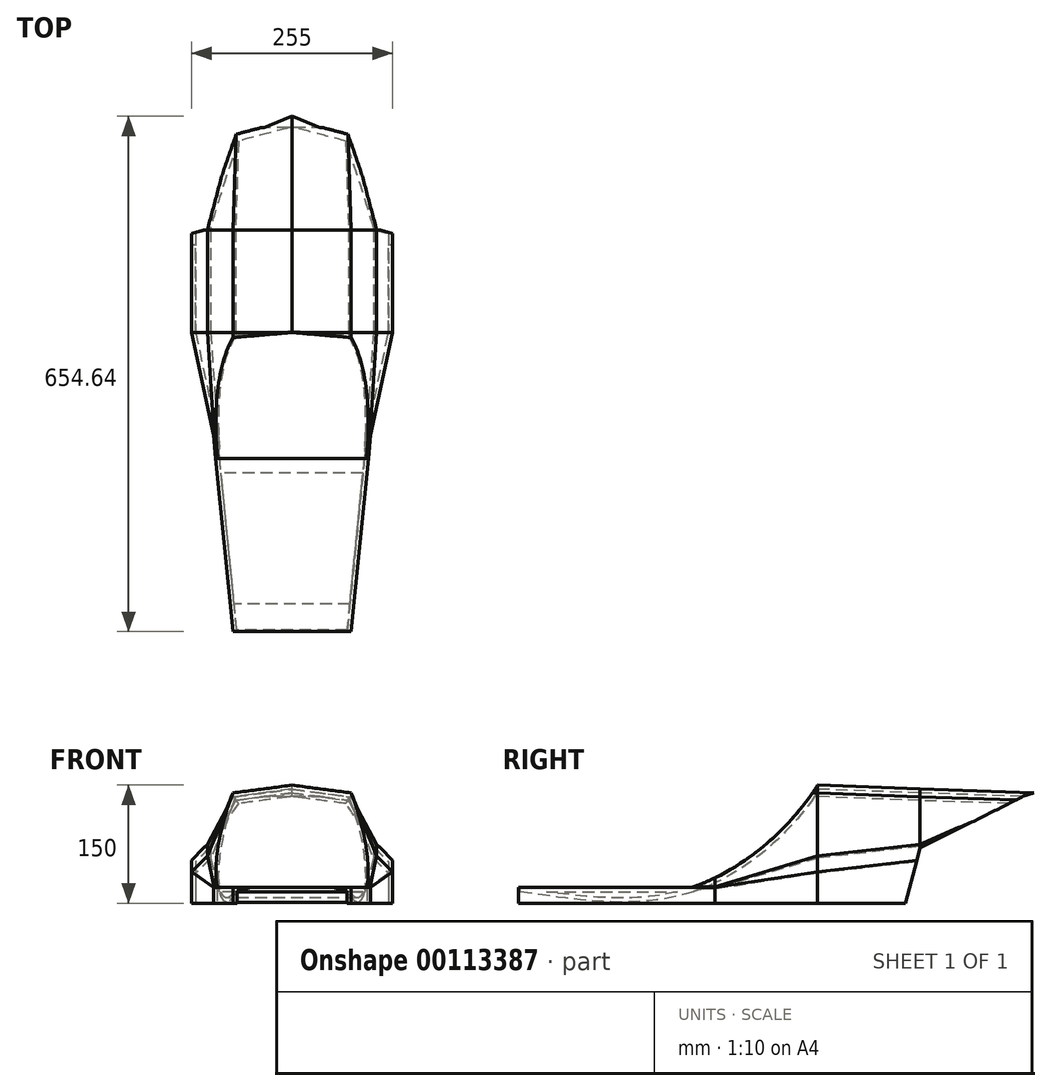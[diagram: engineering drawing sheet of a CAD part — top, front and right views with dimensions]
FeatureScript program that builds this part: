
annotation { "Feature Type Name" : "Feature", "Feature Type Description" : "" }
export const myFeature = defineFeature(function(context is Context, id is Id, definition is map)
    precondition{}
    {
        {
            var Q0;
            Q0=qCreatedBy(makeId("Front.planeOp"),FACE);
            cPlane(context, id + "F0", {"entities" : qUnion([Q0]), "cplaneType" : CPlaneType.OFFSET, "offset" : 380 * mm, "oppositeDirection" : true, "width" : 150 * mm, "height" : 150 * mm});
        }
        {
            var Q0;
            Q0=qCreatedBy(id+"F0.planeOp",FACE);
            cPlane(context, id + "F1", {"entities" : qUnion([Q0]), "cplaneType" : CPlaneType.OFFSET, "offset" : 130 * mm, "oppositeDirection" : true, "width" : 150 * mm, "height" : 150 * mm});
        }
        {
            var Q0;
            Q0=qCreatedBy(id+"F1.planeOp",FACE);
            cPlane(context, id + "F2", {"entities" : qUnion([Q0]), "cplaneType" : CPlaneType.OFFSET, "offset" : 150 * mm, "oppositeDirection" : true, "width" : 150 * mm, "height" : 150 * mm});
        }
        {
            var Q0;
            Q0=qCreatedBy(makeId("Front.planeOp"),FACE);
            cPlane(context, id + "F3", {"entities" : qUnion([Q0]), "cplaneType" : CPlaneType.OFFSET, "offset" : 250 * mm, "oppositeDirection" : true, "width" : 150 * mm, "height" : 150 * mm});
        }
        {
            var Q0;
            Q0=qCreatedBy(id+"F2.planeOp",FACE);
            var sketch = newSketch(context, id + "F4", { "sketchPlane" : qUnion([Q0])});
            skLineSegment(sketch, "E0.bottom", {"start": v(0, 0) * mm, "end": v(-127.5, 0) * mm, "construction": true});
            skLineSegment(sketch, "E0.top", {"start": v(0, 160) * mm, "end": v(-127.5, 160) * mm, "construction": true});
            skLineSegment(sketch, "E0.left", {"start": v(0, 0) * mm, "end": v(0, 160) * mm, "construction": true});
            skLineSegment(sketch, "E0.right", {"start": v(-127.5, 0) * mm, "end": v(-127.5, 160) * mm, "construction": true});
            skLineSegment(sketch, "E1.bottom", {"start": v(0, 160) * mm, "end": v(-70, 160) * mm, "construction": true});
            skLineSegment(sketch, "E1.top", {"start": v(0, 150) * mm, "end": v(-70, 150) * mm, "construction": true});
            skLineSegment(sketch, "E1.left", {"start": v(0, 160) * mm, "end": v(0, 150) * mm, "construction": true});
            skLineSegment(sketch, "E1.right", {"start": v(-70, 160) * mm, "end": v(-70, 150) * mm, "construction": true});
            skLineSegment(sketch, "E2.bottom", {"start": v(-127.5, 0) * mm, "end": v(-107.5, 0) * mm, "construction": true});
            skLineSegment(sketch, "E2.top", {"start": v(-127.5, 65) * mm, "end": v(-107.5, 65) * mm, "construction": true});
            skLineSegment(sketch, "E2.left", {"start": v(-127.5, 0) * mm, "end": v(-127.5, 65) * mm, "construction": true});
            skLineSegment(sketch, "E2.right", {"start": v(-107.5, 0) * mm, "end": v(-107.5, 65) * mm, "construction": true});
            skLineSegment(sketch, "E3.bottom", {"start": v(-107.5, 65) * mm, "end": v(-87.5, 65) * mm, "construction": true});
            skLineSegment(sketch, "E3.top", {"start": v(-107.5, 90) * mm, "end": v(-87.5, 90) * mm, "construction": true});
            skLineSegment(sketch, "E3.left", {"start": v(-107.5, 65) * mm, "end": v(-107.5, 90) * mm, "construction": true});
            skLineSegment(sketch, "E3.right", {"start": v(-87.5, 65) * mm, "end": v(-87.5, 90) * mm, "construction": true});
            skLineSegment(sketch, "E4", {"start": v(0, 160) * mm, "end": v(-70, 150) * mm});
            skLineSegment(sketch, "E5", {"start": v(-70, 150) * mm, "end": v(-107.5, 90) * mm});
            skLineSegment(sketch, "E6", {"start": v(-107.5, 90) * mm, "end": v(-127.5, 65) * mm});
            skLineSegment(sketch, "E7", {"start": v(-127.5, 65) * mm, "end": v(-127.5, 0) * mm});
            skLineSegment(sketch, "E8.MirrorCS", {"start": v(127.5, 0) * mm, "end": v(107.5, 0) * mm, "construction": true});
            skLineSegment(sketch, "E9.MirrorCS", {"start": v(127.5, 0) * mm, "end": v(127.5, 65) * mm, "construction": true});
            skLineSegment(sketch, "E10.MirrorCS", {"start": v(70, 160) * mm, "end": v(70, 150) * mm, "construction": true});
            skLineSegment(sketch, "E11.MirrorCS", {"start": v(0, 150) * mm, "end": v(70, 150) * mm, "construction": true});
            skLineSegment(sketch, "E12.MirrorCS", {"start": v(0, 160) * mm, "end": v(70, 160) * mm, "construction": true});
            skLineSegment(sketch, "E13.MirrorCS", {"start": v(127.5, 65) * mm, "end": v(107.5, 65) * mm, "construction": true});
            skLineSegment(sketch, "E14.MirrorCS", {"start": v(127.5, 0) * mm, "end": v(127.5, 160) * mm, "construction": true});
            skLineSegment(sketch, "E15.MirrorCS", {"start": v(0, 160) * mm, "end": v(127.5, 160) * mm, "construction": true});
            skLineSegment(sketch, "E16.MirrorCS", {"start": v(0, 0) * mm, "end": v(127.5, 0) * mm, "construction": true});
            skLineSegment(sketch, "E17.MirrorCS", {"start": v(87.5, 65) * mm, "end": v(87.5, 90) * mm, "construction": true});
            skLineSegment(sketch, "E18.MirrorCS", {"start": v(127.5, 65) * mm, "end": v(127.5, 0) * mm});
            skLineSegment(sketch, "E19.MirrorCS", {"start": v(107.5, 0) * mm, "end": v(107.5, 65) * mm, "construction": true});
            skLineSegment(sketch, "E20.MirrorCS", {"start": v(107.5, 65) * mm, "end": v(87.5, 65) * mm, "construction": true});
            skLineSegment(sketch, "E21.MirrorCS", {"start": v(0, 160) * mm, "end": v(70, 150) * mm});
            skLineSegment(sketch, "E22.MirrorCS", {"start": v(107.5, 65) * mm, "end": v(107.5, 90) * mm, "construction": true});
            skLineSegment(sketch, "E23.MirrorCS", {"start": v(107.5, 90) * mm, "end": v(87.5, 90) * mm, "construction": true});
            skLineSegment(sketch, "E24.MirrorCS", {"start": v(70, 150) * mm, "end": v(107.5, 90) * mm});
            skLineSegment(sketch, "E25.MirrorCS", {"start": v(107.5, 90) * mm, "end": v(127.5, 65) * mm});
            skLineSegment(sketch, "E26.0", {"start": v(122.5, 63.25) * mm, "end": v(122.5, 0) * mm});
            skLineSegment(sketch, "E26.1", {"start": v(103.41, 87.1) * mm, "end": v(122.5, 63.25) * mm});
            skLineSegment(sketch, "E26.2", {"start": v(67, 145.38) * mm, "end": v(103.41, 87.1) * mm});
            skLineSegment(sketch, "E26.3", {"start": v(0, 154.95) * mm, "end": v(67, 145.38) * mm});
            skLineSegment(sketch, "E26.4", {"start": v(-122.5, 63.25) * mm, "end": v(-122.5, 0) * mm});
            skLineSegment(sketch, "E26.5", {"start": v(-103.41, 87.1) * mm, "end": v(-122.5, 63.25) * mm});
            skLineSegment(sketch, "E26.6", {"start": v(-67, 145.38) * mm, "end": v(-103.41, 87.1) * mm});
            skLineSegment(sketch, "E26.7", {"start": v(0, 154.95) * mm, "end": v(-67, 145.38) * mm});
            skLineSegment(sketch, "E27", {"start": v(127.5, 0) * mm, "end": v(122.5, 0) * mm});
            skLineSegment(sketch, "E28", {"start": v(-122.5, 0) * mm, "end": v(-127.5, 0) * mm});
            skSolve(sketch);
        }
        {
            var Q0;
            Q0=qCreatedBy(id+"F1.planeOp",FACE);
            var sketch = newSketch(context, id + "F5", { "sketchPlane" : qUnion([Q0])});
            skLineSegment(sketch, "E29.bottom", {"start": v(0, 0) * mm, "end": v(-127.5, 0) * mm, "construction": true});
            skLineSegment(sketch, "E29.top", {"start": v(0, 165) * mm, "end": v(-127.5, 165) * mm, "construction": true});
            skLineSegment(sketch, "E29.left", {"start": v(0, 0) * mm, "end": v(0, 165) * mm, "construction": true});
            skLineSegment(sketch, "E29.right", {"start": v(-127.5, 0) * mm, "end": v(-127.5, 165) * mm, "construction": true});
            skLineSegment(sketch, "E30.bottom", {"start": v(0, 165) * mm, "end": v(-75, 165) * mm, "construction": true});
            skLineSegment(sketch, "E30.top", {"start": v(0, 155) * mm, "end": v(-75, 155) * mm, "construction": true});
            skLineSegment(sketch, "E30.left", {"start": v(0, 165) * mm, "end": v(0, 155) * mm, "construction": true});
            skLineSegment(sketch, "E30.right", {"start": v(-75, 165) * mm, "end": v(-75, 155) * mm, "construction": true});
            skLineSegment(sketch, "E31.bottom", {"start": v(-127.5, 0) * mm, "end": v(-107.5, 0) * mm, "construction": true});
            skLineSegment(sketch, "E31.top", {"start": v(-127.5, 75) * mm, "end": v(-107.5, 75) * mm, "construction": true});
            skLineSegment(sketch, "E31.left", {"start": v(-127.5, 0) * mm, "end": v(-127.5, 75) * mm, "construction": true});
            skLineSegment(sketch, "E31.right", {"start": v(-107.5, 0) * mm, "end": v(-107.5, 75) * mm, "construction": true});
            skLineSegment(sketch, "E32.bottom", {"start": v(-107.5, 75) * mm, "end": v(-87.5, 75) * mm, "construction": true});
            skLineSegment(sketch, "E32.top", {"start": v(-107.5, 95) * mm, "end": v(-87.5, 95) * mm, "construction": true});
            skLineSegment(sketch, "E32.left", {"start": v(-107.5, 75) * mm, "end": v(-107.5, 95) * mm, "construction": true});
            skLineSegment(sketch, "E32.right", {"start": v(-87.5, 75) * mm, "end": v(-87.5, 95) * mm, "construction": true});
            skLineSegment(sketch, "E33", {"start": v(0, 165) * mm, "end": v(-75, 155) * mm});
            skLineSegment(sketch, "E34", {"start": v(-75, 155) * mm, "end": v(-107.5, 95) * mm});
            skLineSegment(sketch, "E35", {"start": v(-107.5, 95) * mm, "end": v(-127.5, 75) * mm});
            skLineSegment(sketch, "E36", {"start": v(-127.5, 75) * mm, "end": v(-127.5, 0) * mm});
            skLineSegment(sketch, "E37.MirrorCS", {"start": v(127.5, 0) * mm, "end": v(107.5, 0) * mm, "construction": true});
            skLineSegment(sketch, "E38.MirrorCS", {"start": v(127.5, 0) * mm, "end": v(127.5, 75) * mm, "construction": true});
            skLineSegment(sketch, "E39.MirrorCS", {"start": v(75, 165) * mm, "end": v(75, 155) * mm, "construction": true});
            skLineSegment(sketch, "E40.MirrorCS", {"start": v(0, 155) * mm, "end": v(75, 155) * mm, "construction": true});
            skLineSegment(sketch, "E41.MirrorCS", {"start": v(0, 165) * mm, "end": v(75, 165) * mm, "construction": true});
            skLineSegment(sketch, "E42.MirrorCS", {"start": v(127.5, 75) * mm, "end": v(107.5, 75) * mm, "construction": true});
            skLineSegment(sketch, "E43.MirrorCS", {"start": v(127.5, 0) * mm, "end": v(127.5, 165) * mm, "construction": true});
            skLineSegment(sketch, "E44.MirrorCS", {"start": v(0, 165) * mm, "end": v(127.5, 165) * mm, "construction": true});
            skLineSegment(sketch, "E45.MirrorCS", {"start": v(0, 0) * mm, "end": v(127.5, 0) * mm, "construction": true});
            skLineSegment(sketch, "E46.MirrorCS", {"start": v(87.5, 75) * mm, "end": v(87.5, 95) * mm, "construction": true});
            skLineSegment(sketch, "E47.MirrorCS", {"start": v(127.5, 75) * mm, "end": v(127.5, 0) * mm});
            skLineSegment(sketch, "E48.MirrorCS", {"start": v(107.5, 0) * mm, "end": v(107.5, 75) * mm, "construction": true});
            skLineSegment(sketch, "E49.MirrorCS", {"start": v(107.5, 75) * mm, "end": v(87.5, 75) * mm, "construction": true});
            skLineSegment(sketch, "E50.MirrorCS", {"start": v(0, 165) * mm, "end": v(75, 155) * mm});
            skLineSegment(sketch, "E51.MirrorCS", {"start": v(107.5, 75) * mm, "end": v(107.5, 95) * mm, "construction": true});
            skLineSegment(sketch, "E52.MirrorCS", {"start": v(107.5, 95) * mm, "end": v(87.5, 95) * mm, "construction": true});
            skLineSegment(sketch, "E53.MirrorCS", {"start": v(75, 155) * mm, "end": v(107.5, 95) * mm});
            skLineSegment(sketch, "E54.MirrorCS", {"start": v(107.5, 95) * mm, "end": v(127.5, 75) * mm});
            skLineSegment(sketch, "E55.0", {"start": v(122.5, 72.93) * mm, "end": v(122.5, 0) * mm});
            skLineSegment(sketch, "E55.1", {"start": v(103.45, 91.98) * mm, "end": v(122.5, 72.93) * mm});
            skLineSegment(sketch, "E55.2", {"start": v(71.82, 150.38) * mm, "end": v(103.45, 91.98) * mm});
            skLineSegment(sketch, "E55.3", {"start": v(0, 159.96) * mm, "end": v(71.82, 150.38) * mm});
            skLineSegment(sketch, "E55.4", {"start": v(-122.5, 72.93) * mm, "end": v(-122.5, 0) * mm});
            skLineSegment(sketch, "E55.5", {"start": v(-103.45, 91.98) * mm, "end": v(-122.5, 72.93) * mm});
            skLineSegment(sketch, "E55.6", {"start": v(-71.82, 150.38) * mm, "end": v(-103.45, 91.98) * mm});
            skLineSegment(sketch, "E55.7", {"start": v(0, 159.96) * mm, "end": v(-71.82, 150.38) * mm});
            skLineSegment(sketch, "E56", {"start": v(127.5, 0) * mm, "end": v(122.5, 0) * mm});
            skLineSegment(sketch, "E57", {"start": v(-122.5, 0) * mm, "end": v(-127.5, 0) * mm});
            skSolve(sketch);
        }
        {
            var Q0;
            Q0=qCreatedBy(id+"F0.planeOp",FACE);
            var sketch = newSketch(context, id + "F6", { "sketchPlane" : qUnion([Q0])});
            skLineSegment(sketch, "E58.bottom", {"start": v(0, 0) * mm, "end": v(-127.5, 0) * mm, "construction": true});
            skLineSegment(sketch, "E58.top", {"start": v(0, 170) * mm, "end": v(-127.5, 170) * mm, "construction": true});
            skLineSegment(sketch, "E58.left", {"start": v(0, 0) * mm, "end": v(0, 170) * mm, "construction": true});
            skLineSegment(sketch, "E58.right", {"start": v(-127.5, 0) * mm, "end": v(-127.5, 170) * mm, "construction": true});
            skLineSegment(sketch, "E59.bottom", {"start": v(0, 170) * mm, "end": v(-75, 170) * mm, "construction": true});
            skLineSegment(sketch, "E59.top", {"start": v(0, 160) * mm, "end": v(-75, 160) * mm, "construction": true});
            skLineSegment(sketch, "E59.left", {"start": v(0, 170) * mm, "end": v(0, 160) * mm, "construction": true});
            skLineSegment(sketch, "E59.right", {"start": v(-75, 170) * mm, "end": v(-75, 160) * mm, "construction": true});
            skLineSegment(sketch, "E60.bottom", {"start": v(-127.5, 0) * mm, "end": v(-107.5, 0) * mm, "construction": true});
            skLineSegment(sketch, "E60.top", {"start": v(-127.5, 60) * mm, "end": v(-107.5, 60) * mm, "construction": true});
            skLineSegment(sketch, "E60.left", {"start": v(-127.5, 0) * mm, "end": v(-127.5, 60) * mm, "construction": true});
            skLineSegment(sketch, "E60.right", {"start": v(-107.5, 0) * mm, "end": v(-107.5, 60) * mm, "construction": true});
            skLineSegment(sketch, "E61.bottom", {"start": v(-107.5, 60) * mm, "end": v(-87.5, 60) * mm, "construction": true});
            skLineSegment(sketch, "E61.top", {"start": v(-107.5, 80) * mm, "end": v(-87.5, 80) * mm, "construction": true});
            skLineSegment(sketch, "E61.left", {"start": v(-107.5, 60) * mm, "end": v(-107.5, 80) * mm, "construction": true});
            skLineSegment(sketch, "E61.right", {"start": v(-87.5, 60) * mm, "end": v(-87.5, 80) * mm, "construction": true});
            skLineSegment(sketch, "E62", {"start": v(0, 170) * mm, "end": v(-75, 160) * mm});
            skLineSegment(sketch, "E63", {"start": v(-75, 160) * mm, "end": v(-107.5, 80) * mm});
            skLineSegment(sketch, "E64", {"start": v(-107.5, 80) * mm, "end": v(-127.5, 60) * mm});
            skLineSegment(sketch, "E65", {"start": v(-127.5, 60) * mm, "end": v(-127.5, 0) * mm});
            skLineSegment(sketch, "E66.MirrorCS", {"start": v(127.5, 0) * mm, "end": v(107.5, 0) * mm, "construction": true});
            skLineSegment(sketch, "E67.MirrorCS", {"start": v(127.5, 0) * mm, "end": v(127.5, 60) * mm, "construction": true});
            skLineSegment(sketch, "E68.MirrorCS", {"start": v(75, 170) * mm, "end": v(75, 160) * mm, "construction": true});
            skLineSegment(sketch, "E69.MirrorCS", {"start": v(0, 160) * mm, "end": v(75, 160) * mm, "construction": true});
            skLineSegment(sketch, "E70.MirrorCS", {"start": v(0, 170) * mm, "end": v(75, 170) * mm, "construction": true});
            skLineSegment(sketch, "E71.MirrorCS", {"start": v(127.5, 60) * mm, "end": v(107.5, 60) * mm, "construction": true});
            skLineSegment(sketch, "E72.MirrorCS", {"start": v(127.5, 0) * mm, "end": v(127.5, 170) * mm, "construction": true});
            skLineSegment(sketch, "E73.MirrorCS", {"start": v(0, 170) * mm, "end": v(127.5, 170) * mm, "construction": true});
            skLineSegment(sketch, "E74.MirrorCS", {"start": v(0, 0) * mm, "end": v(127.5, 0) * mm, "construction": true});
            skLineSegment(sketch, "E75.MirrorCS", {"start": v(87.5, 60) * mm, "end": v(87.5, 80) * mm, "construction": true});
            skLineSegment(sketch, "E76.MirrorCS", {"start": v(127.5, 60) * mm, "end": v(127.5, 0) * mm});
            skLineSegment(sketch, "E77.MirrorCS", {"start": v(107.5, 0) * mm, "end": v(107.5, 60) * mm, "construction": true});
            skLineSegment(sketch, "E78.MirrorCS", {"start": v(107.5, 60) * mm, "end": v(87.5, 60) * mm, "construction": true});
            skLineSegment(sketch, "E79.MirrorCS", {"start": v(0, 170) * mm, "end": v(75, 160) * mm});
            skLineSegment(sketch, "E80.MirrorCS", {"start": v(107.5, 60) * mm, "end": v(107.5, 80) * mm, "construction": true});
            skLineSegment(sketch, "E81.MirrorCS", {"start": v(107.5, 80) * mm, "end": v(87.5, 80) * mm, "construction": true});
            skLineSegment(sketch, "E82.MirrorCS", {"start": v(75, 160) * mm, "end": v(107.5, 80) * mm});
            skLineSegment(sketch, "E83.MirrorCS", {"start": v(107.5, 80) * mm, "end": v(127.5, 60) * mm});
            skLineSegment(sketch, "E84.0", {"start": v(122.5, 57.93) * mm, "end": v(122.5, 0) * mm});
            skLineSegment(sketch, "E84.1", {"start": v(103.25, 77.18) * mm, "end": v(122.5, 57.93) * mm});
            skLineSegment(sketch, "E84.2", {"start": v(71.46, 155.43) * mm, "end": v(103.25, 77.18) * mm});
            skLineSegment(sketch, "E84.3", {"start": v(0, 164.96) * mm, "end": v(71.46, 155.43) * mm});
            skLineSegment(sketch, "E84.4", {"start": v(-122.5, 57.93) * mm, "end": v(-122.5, 0) * mm});
            skLineSegment(sketch, "E84.5", {"start": v(-103.25, 77.18) * mm, "end": v(-122.5, 57.93) * mm});
            skLineSegment(sketch, "E84.6", {"start": v(-71.46, 155.43) * mm, "end": v(-103.25, 77.18) * mm});
            skLineSegment(sketch, "E84.7", {"start": v(0, 164.96) * mm, "end": v(-71.46, 155.43) * mm});
            skLineSegment(sketch, "E85", {"start": v(127.5, 0) * mm, "end": v(122.5, 0) * mm});
            skLineSegment(sketch, "E86", {"start": v(-122.5, 0) * mm, "end": v(-127.5, 0) * mm});
            skSolve(sketch);
        }
        {
            var Q0;
            Q0=qCreatedBy(id+"F3.planeOp",FACE);
            var sketch = newSketch(context, id + "F7", { "sketchPlane" : qUnion([Q0])});
            skLineSegment(sketch, "E87.bottom", {"start": v(0, 0) * mm, "end": v(-100, 0) * mm, "construction": true});
            skLineSegment(sketch, "E87.top", {"start": v(0, 170) * mm, "end": v(-100, 170) * mm, "construction": true});
            skLineSegment(sketch, "E87.left", {"start": v(0, 0) * mm, "end": v(0, 170) * mm, "construction": true});
            skLineSegment(sketch, "E87.right", {"start": v(-100, 0) * mm, "end": v(-100, 170) * mm, "construction": true});
            skLineSegment(sketch, "E88.bottom", {"start": v(0, 170) * mm, "end": v(-75, 170) * mm, "construction": true});
            skLineSegment(sketch, "E88.top", {"start": v(0, 160) * mm, "end": v(-75, 160) * mm, "construction": true});
            skLineSegment(sketch, "E88.left", {"start": v(0, 170) * mm, "end": v(0, 160) * mm, "construction": true});
            skLineSegment(sketch, "E88.right", {"start": v(-75, 170) * mm, "end": v(-75, 160) * mm, "construction": true});
            skLineSegment(sketch, "E89.bottom", {"start": v(-100, 0) * mm, "end": v(-99, 0) * mm, "construction": true});
            skLineSegment(sketch, "E89.top", {"start": v(-100, 40) * mm, "end": v(-99, 40) * mm, "construction": true});
            skLineSegment(sketch, "E89.left", {"start": v(-100, 0) * mm, "end": v(-100, 40) * mm, "construction": true});
            skLineSegment(sketch, "E89.right", {"start": v(-99, 0) * mm, "end": v(-99, 40) * mm, "construction": true});
            skLineSegment(sketch, "E90.bottom", {"start": v(-99, 40) * mm, "end": v(-79, 40) * mm, "construction": true});
            skLineSegment(sketch, "E90.top", {"start": v(-99, 41) * mm, "end": v(-79, 41) * mm, "construction": true});
            skLineSegment(sketch, "E90.left", {"start": v(-99, 40) * mm, "end": v(-99, 41) * mm, "construction": true});
            skLineSegment(sketch, "E90.right", {"start": v(-79, 40) * mm, "end": v(-79, 41) * mm, "construction": true});
            skLineSegment(sketch, "E91", {"start": v(0, 170) * mm, "end": v(-75, 160) * mm});
            skLineSegment(sketch, "E92", {"start": v(-75, 160) * mm, "end": v(-99, 41) * mm});
            skLineSegment(sketch, "E93", {"start": v(-99, 41) * mm, "end": v(-100, 40) * mm});
            skLineSegment(sketch, "E94", {"start": v(-100, 40) * mm, "end": v(-100, 0) * mm});
            skLineSegment(sketch, "E95.MirrorCS", {"start": v(100, 0) * mm, "end": v(99, 0) * mm, "construction": true});
            skLineSegment(sketch, "E96.MirrorCS", {"start": v(100, 0) * mm, "end": v(100, 40) * mm, "construction": true});
            skLineSegment(sketch, "E97.MirrorCS", {"start": v(75, 170) * mm, "end": v(75, 160) * mm, "construction": true});
            skLineSegment(sketch, "E98.MirrorCS", {"start": v(0, 160) * mm, "end": v(75, 160) * mm, "construction": true});
            skLineSegment(sketch, "E99.MirrorCS", {"start": v(0, 170) * mm, "end": v(75, 170) * mm, "construction": true});
            skLineSegment(sketch, "E100.MirrorCS", {"start": v(100, 40) * mm, "end": v(99, 40) * mm, "construction": true});
            skLineSegment(sketch, "E101.MirrorCS", {"start": v(100, 0) * mm, "end": v(100, 170) * mm, "construction": true});
            skLineSegment(sketch, "E102.MirrorCS", {"start": v(0, 170) * mm, "end": v(100, 170) * mm, "construction": true});
            skLineSegment(sketch, "E103.MirrorCS", {"start": v(0, 0) * mm, "end": v(100, 0) * mm, "construction": true});
            skLineSegment(sketch, "E104.MirrorCS", {"start": v(79, 40) * mm, "end": v(79, 41) * mm, "construction": true});
            skLineSegment(sketch, "E105.MirrorCS", {"start": v(100, 40) * mm, "end": v(100, 0) * mm});
            skLineSegment(sketch, "E106.MirrorCS", {"start": v(99, 0) * mm, "end": v(99, 40) * mm, "construction": true});
            skLineSegment(sketch, "E107.MirrorCS", {"start": v(99, 40) * mm, "end": v(79, 40) * mm, "construction": true});
            skLineSegment(sketch, "E108.MirrorCS", {"start": v(0, 170) * mm, "end": v(75, 160) * mm});
            skLineSegment(sketch, "E109.MirrorCS", {"start": v(99, 40) * mm, "end": v(99, 41) * mm, "construction": true});
            skLineSegment(sketch, "E110.MirrorCS", {"start": v(99, 41) * mm, "end": v(79, 41) * mm, "construction": true});
            skLineSegment(sketch, "E111.MirrorCS", {"start": v(75, 160) * mm, "end": v(99, 41) * mm});
            skLineSegment(sketch, "E112.MirrorCS", {"start": v(99, 41) * mm, "end": v(100, 40) * mm});
            skLineSegment(sketch, "E113.0", {"start": v(95, 37.93) * mm, "end": v(95, 0) * mm});
            skLineSegment(sketch, "E113.1", {"start": v(94.4, 38.53) * mm, "end": v(95, 37.93) * mm});
            skLineSegment(sketch, "E113.2", {"start": v(70.8, 155.52) * mm, "end": v(94.4, 38.53) * mm});
            skLineSegment(sketch, "E113.3", {"start": v(0, 164.96) * mm, "end": v(70.8, 155.52) * mm});
            skLineSegment(sketch, "E113.4", {"start": v(-95, 37.93) * mm, "end": v(-95, 0) * mm});
            skLineSegment(sketch, "E113.5", {"start": v(-94.4, 38.53) * mm, "end": v(-95, 37.93) * mm});
            skLineSegment(sketch, "E113.6", {"start": v(-70.8, 155.52) * mm, "end": v(-94.4, 38.53) * mm});
            skLineSegment(sketch, "E113.7", {"start": v(0, 164.96) * mm, "end": v(-70.8, 155.52) * mm});
            skLineSegment(sketch, "E114", {"start": v(100, 0) * mm, "end": v(95, 0) * mm});
            skLineSegment(sketch, "E115", {"start": v(-95, 0) * mm, "end": v(-100, 0) * mm});
            skSolve(sketch);
        }
        {
            var Q0;
            Q0=qCreatedBy(makeId("Front.planeOp"),FACE);
            var sketch = newSketch(context, id + "F8", { "sketchPlane" : qUnion([Q0])});
            skLineSegment(sketch, "E116.bottom", {"start": v(0, 0) * mm, "end": v(-75, 0) * mm, "construction": true});
            skLineSegment(sketch, "E116.top", {"start": v(0, 170) * mm, "end": v(-75, 170) * mm, "construction": true});
            skLineSegment(sketch, "E116.left", {"start": v(0, 0) * mm, "end": v(0, 170) * mm, "construction": true});
            skLineSegment(sketch, "E116.right", {"start": v(-75, 0) * mm, "end": v(-75, 170) * mm, "construction": true});
            skLineSegment(sketch, "E117.bottom", {"start": v(0, 170) * mm, "end": v(-30, 170) * mm, "construction": true});
            skLineSegment(sketch, "E117.top", {"start": v(0, 160) * mm, "end": v(-30, 160) * mm, "construction": true});
            skLineSegment(sketch, "E117.left", {"start": v(0, 170) * mm, "end": v(0, 160) * mm, "construction": true});
            skLineSegment(sketch, "E117.right", {"start": v(-30, 170) * mm, "end": v(-30, 160) * mm, "construction": true});
            skLineSegment(sketch, "E118.bottom", {"start": v(-75, 0) * mm, "end": v(-60, 0) * mm, "construction": true});
            skLineSegment(sketch, "E118.top", {"start": v(-75, 40) * mm, "end": v(-60, 40) * mm, "construction": true});
            skLineSegment(sketch, "E118.left", {"start": v(-75, 0) * mm, "end": v(-75, 40) * mm, "construction": true});
            skLineSegment(sketch, "E118.right", {"start": v(-60, 0) * mm, "end": v(-60, 40) * mm, "construction": true});
            skLineSegment(sketch, "E119.bottom", {"start": v(-60, 40) * mm, "end": v(-40, 40) * mm, "construction": true});
            skLineSegment(sketch, "E119.top", {"start": v(-60, 42) * mm, "end": v(-40, 42) * mm, "construction": true});
            skLineSegment(sketch, "E119.left", {"start": v(-60, 40) * mm, "end": v(-60, 42) * mm, "construction": true});
            skLineSegment(sketch, "E119.right", {"start": v(-40, 40) * mm, "end": v(-40, 42) * mm, "construction": true});
            skLineSegment(sketch, "E120", {"start": v(0, 170) * mm, "end": v(-30, 160) * mm});
            skLineSegment(sketch, "E121", {"start": v(-30, 160) * mm, "end": v(-60, 42) * mm});
            skLineSegment(sketch, "E122", {"start": v(-60, 42) * mm, "end": v(-75, 40) * mm});
            skLineSegment(sketch, "E123", {"start": v(-75, 40) * mm, "end": v(-75, 0) * mm});
            skLineSegment(sketch, "E124.MirrorCS", {"start": v(75, 0) * mm, "end": v(60, 0) * mm, "construction": true});
            skLineSegment(sketch, "E125.MirrorCS", {"start": v(75, 0) * mm, "end": v(75, 40) * mm, "construction": true});
            skLineSegment(sketch, "E126.MirrorCS", {"start": v(30, 170) * mm, "end": v(30, 160) * mm, "construction": true});
            skLineSegment(sketch, "E127.MirrorCS", {"start": v(0, 160) * mm, "end": v(30, 160) * mm, "construction": true});
            skLineSegment(sketch, "E128.MirrorCS", {"start": v(0, 170) * mm, "end": v(30, 170) * mm, "construction": true});
            skLineSegment(sketch, "E129.MirrorCS", {"start": v(75, 40) * mm, "end": v(60, 40) * mm, "construction": true});
            skLineSegment(sketch, "E130.MirrorCS", {"start": v(75, 0) * mm, "end": v(75, 170) * mm, "construction": true});
            skLineSegment(sketch, "E131.MirrorCS", {"start": v(0, 170) * mm, "end": v(75, 170) * mm, "construction": true});
            skLineSegment(sketch, "E132.MirrorCS", {"start": v(0, 0) * mm, "end": v(75, 0) * mm, "construction": true});
            skLineSegment(sketch, "E133.MirrorCS", {"start": v(40, 40) * mm, "end": v(40, 42) * mm, "construction": true});
            skLineSegment(sketch, "E134.MirrorCS", {"start": v(75, 40) * mm, "end": v(75, 0) * mm});
            skLineSegment(sketch, "E135.MirrorCS", {"start": v(60, 0) * mm, "end": v(60, 40) * mm, "construction": true});
            skLineSegment(sketch, "E136.MirrorCS", {"start": v(60, 40) * mm, "end": v(40, 40) * mm, "construction": true});
            skLineSegment(sketch, "E137.MirrorCS", {"start": v(0, 170) * mm, "end": v(30, 160) * mm});
            skLineSegment(sketch, "E138.MirrorCS", {"start": v(60, 40) * mm, "end": v(60, 42) * mm, "construction": true});
            skLineSegment(sketch, "E139.MirrorCS", {"start": v(60, 42) * mm, "end": v(40, 42) * mm, "construction": true});
            skLineSegment(sketch, "E140.MirrorCS", {"start": v(30, 160) * mm, "end": v(60, 42) * mm});
            skLineSegment(sketch, "E141.MirrorCS", {"start": v(60, 42) * mm, "end": v(75, 40) * mm});
            skLineSegment(sketch, "E142.0", {"start": v(70, 35.62) * mm, "end": v(70, 0) * mm});
            skLineSegment(sketch, "E142.1", {"start": v(55.99, 37.5) * mm, "end": v(70, 35.62) * mm});
            skLineSegment(sketch, "E142.2", {"start": v(25.83, 156.12) * mm, "end": v(55.99, 37.5) * mm});
            skLineSegment(sketch, "E142.3", {"start": v(0, 164.73) * mm, "end": v(25.83, 156.12) * mm});
            skLineSegment(sketch, "E142.4", {"start": v(-70, 35.62) * mm, "end": v(-70, 0) * mm});
            skLineSegment(sketch, "E142.5", {"start": v(-55.99, 37.5) * mm, "end": v(-70, 35.62) * mm});
            skLineSegment(sketch, "E142.6", {"start": v(-25.83, 156.12) * mm, "end": v(-55.99, 37.5) * mm});
            skLineSegment(sketch, "E142.7", {"start": v(0, 164.73) * mm, "end": v(-25.83, 156.12) * mm});
            skLineSegment(sketch, "E143", {"start": v(75, 0) * mm, "end": v(70, 0) * mm});
            skLineSegment(sketch, "E144", {"start": v(-70, 0) * mm, "end": v(-75, 0) * mm});
            skSolve(sketch);
        }
        {
            var Q0;
            Q0=qCreatedBy(makeId("Right.planeOp"),FACE);
            var sketch = newSketch(context, id + "F9", { "sketchPlane" : qUnion([Q0])});
            skLineSegment(sketch, "E145", {"start": v(0, 0) * mm, "end": v(380, 0) * mm, "construction": true});
            skLineSegment(sketch, "E146", {"start": v(380, 0) * mm, "end": v(380, 170) * mm, "construction": true});
            skLineSegment(sketch, "E147", {"start": v(0, 0) * mm, "end": v(0, 40) * mm, "construction": true});
            skLineSegment(sketch, "E148", {"start": v(0, 40) * mm, "end": v(220, 40) * mm});
            skFitSpline(sketch, "E149", {"points": [v(380, 170) * mm, v(220, 40) * mm, v(0, 40) * mm], "startDerivative": vector(-215.96, -343.22) * mm, "endDerivative": vector(-478.3, 74.11) * mm});
            skLineSegment(sketch, "E150", {"start": v(380, 170) * mm, "end": v(380, 230.78) * mm});
            skLineSegment(sketch, "E151", {"start": v(380, 230.78) * mm, "end": v(7.34, 230.78) * mm});
            skLineSegment(sketch, "E152", {"start": v(7.34, 230.78) * mm, "end": v(-5.55, 185.11) * mm});
            skLineSegment(sketch, "E153", {"start": v(-5.55, 185.11) * mm, "end": v(0, 40) * mm});
            skSolve(sketch);
        }
        {
            var Q0;
            Q0=qCreatedBy(makeId("Right.planeOp"),FACE);
            var sketch = newSketch(context, id + "F10", { "sketchPlane" : qUnion([Q0])});
            skLineSegment(sketch, "E154", {"start": v(0, 0) * mm, "end": v(600, 0) * mm, "construction": true});
            skLineSegment(sketch, "E155", {"start": v(600, 0) * mm, "end": v(600, 40) * mm});
            skLineSegment(sketch, "E156", {"start": v(600, 40) * mm, "end": v(600, 65) * mm, "construction": true});
            skLineSegment(sketch, "E157", {"start": v(600, 65) * mm, "end": v(625, 65) * mm, "construction": true});
            skLineSegment(sketch, "E158", {"start": v(600, 40) * mm, "end": v(625, 65) * mm});
            skLineSegment(sketch, "E159", {"start": v(625, 65) * mm, "end": v(880.62, 212.2) * mm});
            skLineSegment(sketch, "E160", {"start": v(880.62, 212.2) * mm, "end": v(932.67, 242.1) * mm});
            skLineSegment(sketch, "E161", {"start": v(932.67, 242.1) * mm, "end": v(866.28, 117.59) * mm});
            skLineSegment(sketch, "E162", {"start": v(866.28, 117.59) * mm, "end": v(834.8, 61.75) * mm});
            skLineSegment(sketch, "E163", {"start": v(600, 0) * mm, "end": v(790, 0) * mm});
            skLineSegment(sketch, "E164", {"start": v(790, 0) * mm, "end": v(790, 65) * mm, "construction": true});
            skLineSegment(sketch, "E165", {"start": v(834.8, 61.75) * mm, "end": v(790, 0) * mm});
            skSolve(sketch);
        }
        {
            var Q0;
            Q0=qCreatedBy(makeId("Right.planeOp"),FACE);
            var sketch = newSketch(context, id + "F11", { "sketchPlane" : qUnion([Q0])});
            skLineSegment(sketch, "E166", {"start": v(0, 0) * mm, "end": v(380, 0) * mm, "construction": true});
            skLineSegment(sketch, "E167", {"start": v(380, 0) * mm, "end": v(380, 170) * mm, "construction": true});
            skLineSegment(sketch, "E168", {"start": v(0, 0) * mm, "end": v(0, 40) * mm, "construction": true});
            skLineSegment(sketch, "E169", {"start": v(0, 40) * mm, "end": v(220, 40) * mm});
            skFitSpline(sketch, "E170", {"points": [v(380, 170) * mm, v(220, 40) * mm, v(0, 40) * mm], "startDerivative": vector(-215.96, -343.22) * mm, "endDerivative": vector(-478.3, 74.11) * mm});
            skLineSegment(sketch, "E171", {"start": v(2.2, -5.3) * mm, "end": v(382.2, -5.3) * mm, "construction": true});
            skLineSegment(sketch, "E172", {"start": v(382.2, -5.3) * mm, "end": v(382.2, 164.7) * mm, "construction": true});
            skLineSegment(sketch, "E173", {"start": v(2.2, -5.3) * mm, "end": v(2.2, 34.7) * mm, "construction": true});
            skLineSegment(sketch, "E174", {"start": v(2.2, 34.7) * mm, "end": v(222.2, 34.7) * mm});
            skFitSpline(sketch, "E175", {"points": [v(382.2, 164.7) * mm, v(222.2, 34.7) * mm, v(2.2, 34.7) * mm], "startDerivative": vector(-215.96, -343.22) * mm, "endDerivative": vector(-478.3, 74.11) * mm});
            skLineSegment(sketch, "E176", {"start": v(2.2, 34.7) * mm, "end": v(0, 40) * mm});
            skLineSegment(sketch, "E177", {"start": v(382.2, 164.7) * mm, "end": v(380, 170) * mm});
            skSolve(sketch);
        }
        {
            var Q0;
            Q0=qSketchRegion(id+"F5",true);
            var Q1;
            Q1=qSketchRegion(id+"F6",true);
            loft(context, id + "F12", {"sheetProfilesArray" : [{ "sheetProfileEntities" : qUnion([Q0]) }, { "sheetProfileEntities" : qUnion([Q1]) }]});
        }
        {
            var Q0;
            Q0=qCreatedBy(makeId("Top.planeOp"),FACE);
            var sketch = newSketch(context, id + "F13", { "sketchPlane" : qUnion([Q0])});
            skLineSegment(sketch, "E178", {"start": v(0, 0) * mm, "end": v(0, 660) * mm, "construction": true});
            skLineSegment(sketch, "E179", {"start": v(0, 660) * mm, "end": v(-38, 660) * mm, "construction": true});
            skLineSegment(sketch, "E180", {"start": v(0, 640) * mm, "end": v(-71, 640) * mm, "construction": true});
            skLineSegment(sketch, "E181", {"start": v(-38, 660) * mm, "end": v(-71, 640) * mm});
            skLineSegment(sketch, "E182", {"start": v(-71, 640) * mm, "end": v(-71, 610) * mm, "construction": true});
            skLineSegment(sketch, "E183", {"start": v(-71, 610) * mm, "end": v(-81, 610) * mm, "construction": true});
            skLineSegment(sketch, "E184", {"start": v(-71, 640) * mm, "end": v(-81, 610) * mm});
            skLineSegment(sketch, "E185", {"start": v(-81, 610) * mm, "end": v(-81, 605) * mm, "construction": true});
            skLineSegment(sketch, "E186", {"start": v(0, 510) * mm, "end": v(-107.58, 510) * mm, "construction": true});
            skLineSegment(sketch, "E187", {"start": v(-81, 610) * mm, "end": v(-107.58, 510) * mm});
            skLineSegment(sketch, "E188", {"start": v(-107.58, 510) * mm, "end": v(-166.67, 510) * mm});
            skLineSegment(sketch, "E189", {"start": v(-166.67, 510) * mm, "end": v(-157.39, 706.64) * mm});
            skLineSegment(sketch, "E190", {"start": v(-157.39, 706.64) * mm, "end": v(-38, 660) * mm});
            skLineSegment(sketch, "E191.MirrorCS", {"start": v(81, 610) * mm, "end": v(81, 610) * mm});
            skLineSegment(sketch, "E192.MirrorCS", {"start": v(81, 610) * mm, "end": v(81, 605) * mm, "construction": true});
            skLineSegment(sketch, "E193.MirrorCS", {"start": v(81, 605) * mm, "end": v(81, 610) * mm, "construction": true});
            skLineSegment(sketch, "E194.MirrorCS", {"start": v(71, 610) * mm, "end": v(81, 610) * mm, "construction": true});
            skLineSegment(sketch, "E195.MirrorCS", {"start": v(71, 640) * mm, "end": v(71, 610) * mm, "construction": true});
            skLineSegment(sketch, "E196.MirrorCS", {"start": v(0, 660) * mm, "end": v(38, 660) * mm, "construction": true});
            skLineSegment(sketch, "E197.MirrorCS", {"start": v(71, 640) * mm, "end": v(81, 610) * mm});
            skLineSegment(sketch, "E198.MirrorCS", {"start": v(166.67, 510) * mm, "end": v(157.39, 706.64) * mm});
            skLineSegment(sketch, "E199.MirrorCS", {"start": v(0, 640) * mm, "end": v(71, 640) * mm, "construction": true});
            skLineSegment(sketch, "E200.MirrorCS", {"start": v(0, 510) * mm, "end": v(107.58, 510) * mm, "construction": true});
            skLineSegment(sketch, "E201.MirrorCS", {"start": v(38, 660) * mm, "end": v(71, 640) * mm});
            skLineSegment(sketch, "E202.MirrorCS", {"start": v(81, 610) * mm, "end": v(107.58, 510) * mm});
            skLineSegment(sketch, "E203.MirrorCS", {"start": v(157.39, 706.64) * mm, "end": v(38, 660) * mm});
            skLineSegment(sketch, "E204.MirrorCS", {"start": v(107.58, 510) * mm, "end": v(166.67, 510) * mm});
            skSolve(sketch);
        }
        {
            var Q0;
            Q0=qCreatedBy(makeId("Right.planeOp"),FACE);
            var sketch = newSketch(context, id + "F14", { "sketchPlane" : qUnion([Q0])});
            skLineSegment(sketch, "E205", {"start": v(0, 0) * mm, "end": v(0, 20) * mm});
            skLineSegment(sketch, "E206", {"start": v(0, 20) * mm, "end": v(550.35, 20) * mm});
            skLineSegment(sketch, "E207", {"start": v(550.35, 20) * mm, "end": v(550.35, 0) * mm});
            skLineSegment(sketch, "E208", {"start": v(550.35, 0) * mm, "end": v(0, 0) * mm});
            skSolve(sketch);
        }
        {
            var Q0;
            Q0=makeQuery(id+"F9.imprint","IMPRINT",FACE,{"disambiguationData":[TD([[makeQuery(id+"F9.imprint","IMPRINT",EDGE,{"derivedFrom":sQuery(id+"F9.wireOp",EDGE,"E148")}),1.0]])]});
            extrude(context, id + "F15", {"entities" : qUnion([Q0]), "operationType" : NewBodyOperationType.REMOVE, "oppositeDirection" : true, "depth" : 200 * mm, "hasSecondDirection" : true, "secondDirectionOppositeDirection" : false, "secondDirectionDepth" : 200 * mm});
        }
        {
            var Q1;
            Q1 = qSketchRegion(id + "F4", true);
            var Q2;
            Q2 = qSketchRegion(id + "F5", true);
            loft(context, id + "F16", {"operationType" : NewBodyOperationType.ADD, "sheetProfilesArray" : [{ "sheetProfileEntities" : qUnion([Q1]) }, { "sheetProfileEntities" : qUnion([Q2]) }]});
        }
        {
            var Q0;
            Q0 = qSketchRegion(id + "F13", true);
            extrude(context, id + "F17", {"entities" : qUnion([Q0]), "operationType" : NewBodyOperationType.REMOVE, "depth" : 200 * mm});
        }
        {
            var Q0;
            Q0=qCreatedBy(makeId("Right.planeOp"),FACE);
            var sketch = newSketch(context, id + "F18", { "sketchPlane" : qUnion([Q0])});
            skLineSegment(sketch, "E209", {"start": v(0, 0) * mm, "end": v(510, 0) * mm, "construction": true});
            skLineSegment(sketch, "E210", {"start": v(510, 0) * mm, "end": v(510, 90) * mm, "construction": true});
            skLineSegment(sketch, "E211", {"start": v(510, 0) * mm, "end": v(640, 0) * mm});
            skLineSegment(sketch, "E212", {"start": v(640, 0) * mm, "end": v(640, 155) * mm, "construction": true});
            skLineSegment(sketch, "E213", {"start": v(510, 90) * mm, "end": v(640, 155) * mm});
            skLineSegment(sketch, "E214", {"start": v(640, 0) * mm, "end": v(640.2, 0) * mm});
            skLineSegment(sketch, "E215", {"start": v(640.2, 0) * mm, "end": v(640.2, 155.65) * mm, "construction": true});
            skLineSegment(sketch, "E216", {"start": v(640.2, 0) * mm, "end": v(660, 0) * mm});
            skLineSegment(sketch, "E217", {"start": v(660, 0) * mm, "end": v(660, 161.86) * mm});
            skLineSegment(sketch, "E218", {"start": v(640, 155) * mm, "end": v(640.2, 155.65) * mm});
            skLineSegment(sketch, "E219", {"start": v(640.2, 155.65) * mm, "end": v(660, 161.86) * mm});
            skLineSegment(sketch, "E220", {"start": v(510, 90) * mm, "end": v(486.52, 0) * mm});
            skLineSegment(sketch, "E221", {"start": v(486.52, 0) * mm, "end": v(510, 0) * mm});
            skSolve(sketch);
        }
        {
            var Q0;
            Q0=makeQuery(id+"F18.imprint","IMPRINT",FACE,{"disambiguationData":[TD([[makeQuery(id+"F18.imprint","IMPRINT",EDGE,{"derivedFrom":sQuery(id+"F18.wireOp",EDGE,"E211")}),1.0]])]});
            extrude(context, id + "F19", {"entities" : qUnion([Q0]), "operationType" : NewBodyOperationType.REMOVE, "depth" : 200 * mm, "hasSecondDirection" : true, "secondDirectionOppositeDirection" : true, "secondDirectionDepth" : 200 * mm});
        }
        {
            var Q1;
            Q1 = qSketchRegion(id + "F6", true);
            var Q2;
            Q2 = qSketchRegion(id + "F7", true);
            loft(context, id + "F20", {"operationType" : NewBodyOperationType.ADD, "sheetProfilesArray" : [{ "sheetProfileEntities" : qUnion([Q1]) }, { "sheetProfileEntities" : qUnion([Q2]) }]});
        }
        {
            var Q1;
            Q1 = qSketchRegion(id + "F7", true);
            var Q2;
            Q2 = qSketchRegion(id + "F8", true);
            loft(context, id + "F21", {"operationType" : NewBodyOperationType.ADD, "sheetProfilesArray" : [{ "sheetProfileEntities" : qUnion([Q1]) }, { "sheetProfileEntities" : qUnion([Q2]) }]});
        }
        {
            var Q0;
            Q0 = qSketchRegion(id + "F11", true);
            var Q1;
            Q1=makeQuery(id+"F15.boolean.opBoolean","COPY",FACE,{"derivedFrom":makeQuery(id+"F15.opExtrude","SWEPT_FACE",FACE,{"disambiguationData":[OSD([sQuery(id+"F9.wireOp",EDGE,"E149")])]})});
            var Q2;
            Q2=makeQuery(id+"F12.opLoft","SWEPT_BODY",BODY,{"disambiguationData":[OSD([makeQuery(id+"F5.imprint","IMPRINT",FACE,{"disambiguationData":[TD([[makeQuery(id+"F5.imprint","IMPRINT",EDGE,{"derivedFrom":sQuery(id+"F5.wireOp",EDGE,"E33")}),1.0]])]}),makeQuery(id+"F6.imprint","IMPRINT",FACE,{"disambiguationData":[TD([[makeQuery(id+"F6.imprint","IMPRINT",EDGE,{"derivedFrom":sQuery(id+"F6.wireOp",EDGE,"E62")}),1.0]])]})])]});
            var Q3;
            Q3=makeQuery(id+"F12.opLoft","SWEPT_BODY",BODY,{"disambiguationData":[OSD([makeQuery(id+"F5.imprint","IMPRINT",FACE,{"disambiguationData":[TD([[makeQuery(id+"F5.imprint","IMPRINT",EDGE,{"derivedFrom":sQuery(id+"F5.wireOp",EDGE,"E33")}),1.0]])]}),makeQuery(id+"F6.imprint","IMPRINT",FACE,{"disambiguationData":[TD([[makeQuery(id+"F6.imprint","IMPRINT",EDGE,{"derivedFrom":sQuery(id+"F6.wireOp",EDGE,"E62")}),1.0]])]})])]});
            extrude(context, id + "F22", {"entities" : qUnion([Q0]), "operationType" : NewBodyOperationType.ADD, "endBound" : BoundingType.UP_TO_BODY, "endBoundEntityFace" : qUnion([Q1]), "endBoundEntityBody" : qUnion([Q2]), "depth" : 25 * mm, "hasSecondDirection" : true, "secondDirectionBound" : SecondDirectionBoundingType.UP_TO_BODY, "secondDirectionOppositeDirection" : true, "secondDirectionBoundEntityBody" : qUnion([Q3]), "secondDirectionDepth" : 25 * mm});
        }
        {
            var Q0;
            Q0=makeQuery(id+"F9.imprint","IMPRINT",FACE,{"disambiguationData":[TD([[makeQuery(id+"F9.imprint","IMPRINT",EDGE,{"derivedFrom":sQuery(id+"F9.wireOp",EDGE,"E148")}),1.0]])]});
            extrude(context, id + "F23", {"entities" : qUnion([Q0]), "operationType" : NewBodyOperationType.REMOVE, "oppositeDirection" : true, "depth" : 200 * mm, "hasSecondDirection" : true, "secondDirectionOppositeDirection" : false, "secondDirectionDepth" : 200 * mm});
        }
        {
            var Q0;
            Q0=makeQuery(id+"F14.imprint","IMPRINT",FACE,{"disambiguationData":[TD([[makeQuery(id+"F14.imprint","IMPRINT",EDGE,{"derivedFrom":sQuery(id+"F14.wireOp",EDGE,"E205")}),-1.0]])]});
            extrude(context, id + "F24", {"entities" : qUnion([Q0]), "operationType" : NewBodyOperationType.REMOVE, "depth" : 200 * mm, "hasSecondDirection" : true, "secondDirectionOppositeDirection" : true, "secondDirectionDepth" : 200 * mm});
        }
    });
